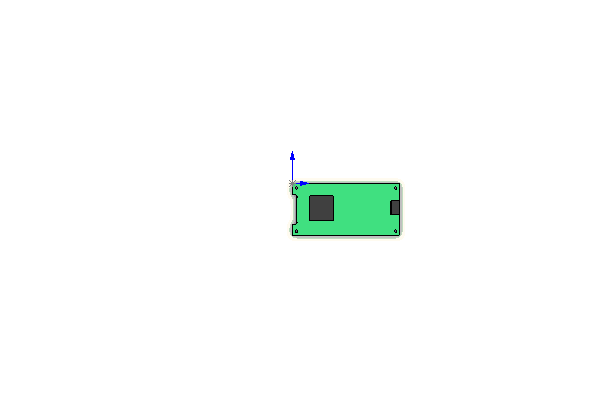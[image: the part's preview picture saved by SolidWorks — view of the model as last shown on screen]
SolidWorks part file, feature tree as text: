
SOLIDWORKS PART (.sldprt)
format: sldprt  version: not decoded by parser v0  size: 254,464 bytes
history: native  units: mm
features: sketch x5, extrude x3, cut_extrude x2, material x1 (+13 scaffold rows collapsed)
feature tree (24):
  scaffold x13  (default folders/planes/origin — collapsed)
  material  "Material <not specified>"
  sketch  "Sketch1"  dims[D1=158.75mm D2=76.2mm]
  extrude  "Extrude1"  Depth=1.5748mm
  sketch  "Sketch2"  dims[c1.D1=~1.999298mm c1.D5=3.81mm c1.D6=3.81mm c1.D11=3.81mm c1.D12=3.81mm c2.D1=6.35mm c2.D2=6.35mm c2.D3=6.35mm c2.D4=6.35mm c2.D7=6.35mm c2.D8=6.35mm c2.D9=6.35mm c2.D10=6.35mm]
  cut_extrude  "Cut-Extrude2"  Depth=1.5748mm
  sketch  "Sketch4"  dims[c1.D1=1.3mm c1.D2=1.3mm c1.D10=1.0mm c1.D11=1.0mm c1.D3=~19.234912mm c1.D4=7.55mm c1.D5=~19.234912mm c1.D6=7.55mm c1.D7=~37.730176mm c1.D8=43.53mm c1.D9=5.95mm c1.D12=~36.528293mm c1.D13=~39.671707mm c2.D12=~16.334994mm c2.D13=~16.335006mm]
  cut_extrude  "Cut-Extrude3"  Depth=1.5748mm
  sketch  "Sketch5"
  extrude  "Extrude2"  Depth=3.302mm
  sketch  "Sketch6"  dims[D1=13.081mm D2=20.574mm]
  extrude  "Extrude3"  Depth=7.874mm
decode coverage: 9 of 10 modeling features carry decoded parameters
note: ~ marks probable driven/reference dimensions
note: suppression state not decoded; provenance and decode notes live in map.json
